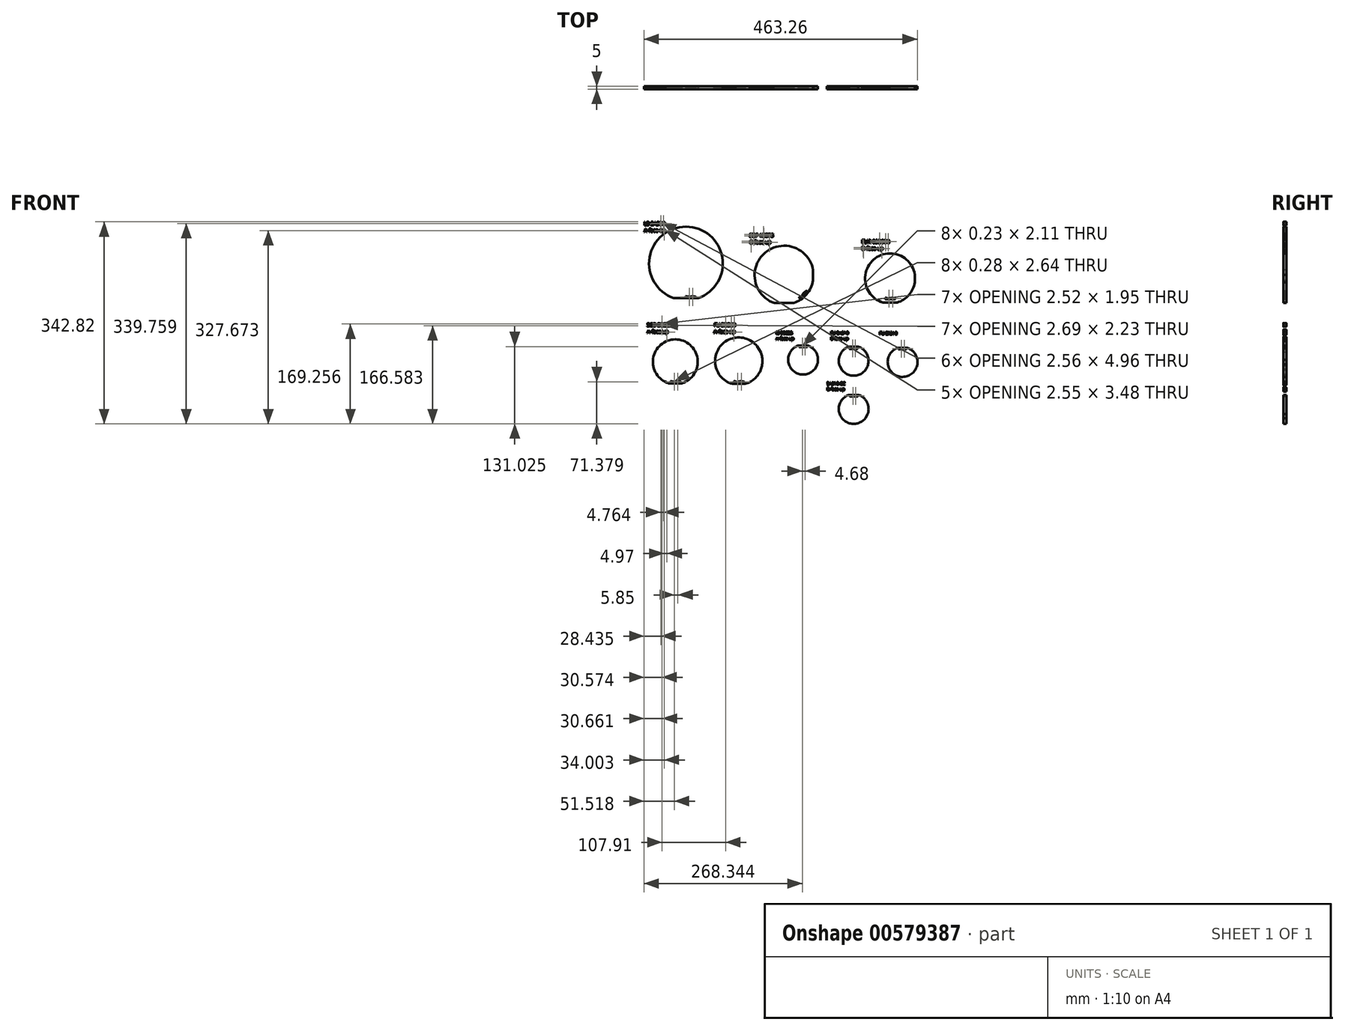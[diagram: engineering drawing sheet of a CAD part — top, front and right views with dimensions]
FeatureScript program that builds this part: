
annotation { "Feature Type Name" : "Feature", "Feature Type Description" : "" }
export const myFeature = defineFeature(function(context is Context, id is Id, definition is map)
    precondition{}
    {
        {
            var Q0;
            Q0=qCreatedBy(makeId("Front.planeOp"),FACE);
            var sketch = newSketch(context, id + "F0", { "sketchPlane" : qUnion([Q0])});
            skArc(sketch, "E0", {"start": v(21, -58.87) * mm, "mid": v(0, 62.5) * mm, "end": v(-21, -58.87) * mm});
            skLineSegment(sketch, "E1", {"start": v(0, -58.87) * mm, "end": v(21, -58.87) * mm});
            skLineSegment(sketch, "E2", {"start": v(21, -58.87) * mm, "end": v(-21, -58.87) * mm});
            skPoint(sketch, "E3.orphan", {"position": v(0, 62.5) * mm});
            skLineSegment(sketch, "E4", {"start": v(0, -58.87) * mm, "end": v(0, -57.87) * mm});
            skText(sketch, "E5", { "text": "Boule-Slice", "fontName": "OpenSans-Regular.ttf"});
            skText(sketch, "E6", { "text": "L3 5A900\nA-face up", "fontName": "OpenSans-Regular.ttf"});
            const initialGuessF0  = {"E5": [-0.00118, -0.05786, 1, 0, 0.0025], "E6": [-0.08084, 0.06549, 1, 0, 0.006]};
            skSetInitialGuess(sketch, initialGuessF0);
            skSolve(sketch);
        }
        {
            var Q0;
            Q0=qCreatedBy(makeId("Front.planeOp"),FACE);
            var sketch = newSketch(context, id + "F1", { "sketchPlane" : qUnion([Q0])});
            skArc(sketch, "E7", {"start": v(182.66, -67.08) * mm, "mid": v(204.4, -52.3) * mm, "end": v(215.64, -28.54) * mm});
            skLineSegment(sketch, "E8", {"start": v(182.66, -67.08) * mm, "end": v(150.16, -67.08) * mm});
            skText(sketch, "E9", { "text": "Boule-Slice", "fontName": "OpenSans-Regular.ttf"});
            skLineSegment(sketch, "E10", {"start": v(215.64, -19.31) * mm, "end": v(215.64, -28.54) * mm});
            skLineSegment(sketch, "E11", {"start": v(215.64, -28.54) * mm, "end": v(215.64, -11.04) * mm});
            skArc(sketch, "E12.trimOffspring", {"start": v(215.64, -11.04) * mm, "mid": v(133.9, 18.2) * mm, "end": v(150.16, -67.08) * mm});
            skArc(sketch, "E13", {"start": v(358.04, -66.17) * mm, "mid": v(378.01, -53.4) * mm, "end": v(388.04, -31.9) * mm});
            skLineSegment(sketch, "E14", {"start": v(358.04, -66.17) * mm, "end": v(334.04, -66.17) * mm});
            skText(sketch, "E15", { "text": "Boule-Slice", "fontName": "OpenSans-Regular.ttf"});
            skLineSegment(sketch, "E16", {"start": v(388.04, -31.9) * mm, "end": v(388.04, -18.9) * mm});
            skArc(sketch, "E17.trimOffspring", {"start": v(388.04, -18.9) * mm, "mid": v(318.04, 6.58) * mm, "end": v(334.04, -66.17) * mm});
            skText(sketch, "E18", { "text": "L3 5A900\nA-face up", "fontName": "OpenSans-Regular.ttf"});
            skText(sketch, "E19", { "text": "SBF 4B875\nB-face up", "fontName": "OpenSans-Regular.ttf"});
            skText(sketch, "E20", { "text": "FLIR 85B900\nB-face up", "fontName": "OpenSans-Regular.ttf"});
            skLineSegment(sketch, "E21", {"start": v(-9.02, -203.08) * mm, "end": v(-7.02, -203.08) * mm});
            skLineSegment(sketch, "E22", {"start": v(-7.02, -203.08) * mm, "end": v(-29.02, -203.08) * mm});
            skText(sketch, "E23", { "text": "Boule-Slice", "fontName": "OpenSans-Regular.ttf"});
            skText(sketch, "E24", { "text": "SCD 3B825\nA-face up", "fontName": "OpenSans-Regular.ttf"});
            skArc(sketch, "E25", {"start": v(-7.02, -203.08) * mm, "mid": v(-18.02, -128.71) * mm, "end": v(-29.02, -203.08) * mm});
            skText(sketch, "E26", { "text": "Boule-Slice", "fontName": "OpenSans-Regular.ttf"});
            skText(sketch, "E27", { "text": "FU 3B800\nA-face up", "fontName": "OpenSans-Regular.ttf"});
            skArc(sketch, "E28", {"start": v(120.92, -140.52) * mm, "mid": v(56.1, -143.31) * mm, "end": v(78.53, -204.2) * mm});
            skLineSegment(sketch, "E29", {"start": v(120.92, -140.52) * mm, "end": v(126.92, -150.9) * mm});
            skLineSegment(sketch, "E30", {"start": v(100.53, -204.2) * mm, "end": v(78.53, -204.2) * mm});
            skArc(sketch, "E31.trimOffspring", {"start": v(100.53, -204.2) * mm, "mid": v(125.52, -183.4) * mm, "end": v(126.92, -150.9) * mm});
            const initialGuessF1  = {"E9": [0.193, -0.05963, 0.7071, 0.7071, 0.0025], "E15": [0.33754, -0.06053, 1, 0, 0.0025], "E18": [-0.07111, 0.06484, 1, 0, 0.006], "E19": [0.10778, 0.04488, 1, 0, 0.006], "E20": [0.29791, 0.0343, 1, 0, 0.006], "E23": [-0.02651, -0.20188, 1, 0, 0.0025], "E24": [-0.06614, -0.10706, 1, 0, 0.006], "E26": [0.08103, -0.20188, 1, 0, 0.0025], "E27": [0.04731, -0.10706, 1, 0, 0.006]};
            skSetInitialGuess(sketch, initialGuessF1);
            skSolve(sketch);
        }
        {
            var Q0;
            Q0=qCreatedBy(makeId("Front.planeOp"),FACE);
            var sketch = newSketch(context, id + "F2", { "sketchPlane" : qUnion([Q0])});
            skArc(sketch, "E32", {"start": v(222.18, -172.07) * mm, "mid": v(221.52, -152.51) * mm, "end": v(207.09, -139.3) * mm});
            skLineSegment(sketch, "E33", {"start": v(222.18, -172.07) * mm, "end": v(218.18, -179) * mm});
            skLineSegment(sketch, "E34", {"start": v(207.09, -139.3) * mm, "end": v(190.09, -139.3) * mm});
            skArc(sketch, "E35.trimOffspring", {"start": v(190.09, -139.3) * mm, "mid": v(177.97, -177.66) * mm, "end": v(218.18, -179) * mm});
            skText(sketch, "E36", { "text": "Boule-Slice", "fontName": "OpenSans-Regular.ttf"});
            skText(sketch, "E37", { "text": "i3 2B625\nA-face up", "fontName": "OpenSans-Regular.ttf"});
            skText(sketch, "E38", { "text": "FU 2A510\nB-face up", "fontName": "OpenSans-Regular.ttf"});
            skLineSegment(sketch, "E39.MirrorCS", {"start": v(260.72, -174.09) * mm, "end": v(264.72, -181.01) * mm});
            skLineSegment(sketch, "E40.MirrorCS", {"start": v(276.31, -141.13) * mm, "end": v(292.31, -141.13) * mm});
            skArc(sketch, "E41.MirrorCS", {"start": v(260.72, -174.09) * mm, "mid": v(261.5, -154.28) * mm, "end": v(276.31, -141.13) * mm});
            skArc(sketch, "E42.MirrorCS", {"start": v(292.31, -141.13) * mm, "mid": v(305.08, -179.45) * mm, "end": v(264.72, -181.01) * mm});
            skText(sketch, "E43", { "text": "Boule-Slice", "fontName": "OpenSans-Regular.ttf"});
            skPoint(sketch, "E44", {"position": v(192.9, -141.97) * mm});
            skText(sketch, "E45", { "text": "FU 2X510\n", "fontName": "OpenSans-Regular.ttf"});
            skLineSegment(sketch, "E46.MirrorCS", {"start": v(359.22, -143.15) * mm, "end": v(375.22, -143.15) * mm});
            skText(sketch, "E47", { "text": "Boule-Slice", "fontName": "OpenSans-Regular.ttf"});
            skLineSegment(sketch, "E48", {"start": v(392.15, -171.1) * mm, "end": v(392.15, -163.1) * mm});
            skArc(sketch, "E49", {"start": v(359.22, -143.15) * mm, "mid": v(350.88, -186.35) * mm, "end": v(392.15, -171.1) * mm});
            skArc(sketch, "E50.trimOffspring", {"start": v(392.15, -163.1) * mm, "mid": v(386.47, -150.76) * mm, "end": v(375.22, -143.15) * mm});
            skArc(sketch, "E51", {"start": v(307.95, -255.69) * mm, "mid": v(307.29, -236.13) * mm, "end": v(292.85, -222.9) * mm});
            skLineSegment(sketch, "E52", {"start": v(307.95, -255.69) * mm, "end": v(303.95, -262.62) * mm});
            skLineSegment(sketch, "E53", {"start": v(292.85, -222.9) * mm, "end": v(275.85, -222.9) * mm});
            skArc(sketch, "E54.trimOffspring", {"start": v(275.85, -222.9) * mm, "mid": v(263.74, -261.27) * mm, "end": v(303.95, -262.62) * mm});
            skText(sketch, "E55", { "text": "Boule-Slice", "fontName": "OpenSans-Regular.ttf"});
            skPoint(sketch, "E56", {"position": v(278.67, -225.58) * mm});
            skText(sketch, "E57", { "text": "2A510-CC\nB-face up", "fontName": "OpenSans-Regular.ttf"});
            const initialGuessF2  = {"E36": [0.1917, -0.14197, 1, 0, 0.002], "E37": [0.1527, -0.12022, 1, 0, 0.005], "E38": [0.24497, -0.12022, 1, 0, 0.005], "E43": [0.2769, -0.14481, 1, 0, 0.002], "E45": [0.32788, -0.12073, 1, 0, 0.005], "E47": [0.3598, -0.14532, 1, 0, 0.002], "E55": [0.27747, -0.22558, 1, 0, 0.002], "E57": [0.23866, -0.20613, 1, 0, 0.005]};
            skSetInitialGuess(sketch, initialGuessF2);
            skSolve(sketch);
        }
        {
            var Q0;
            {var subQ1=sQuery(id+"F0.wireOp",EDGE,"E0");Q0=makeQuery(id+"F0.imprint","IMPRINT",FACE,{"disambiguationData":[TD([[makeQuery(id+"F0.imprint","IMPRINT",EDGE,{"derivedFrom":subQ1}),1.0]])]});}
            var Q1;
            Q1=makeQuery(id+"F0.imprint","IMPRINT",FACE,{"disambiguationData":[TD([[makeQuery(id+"F0.imprint","IMPRINT",EDGE,{"derivedFrom":sQuery(id+"F0.wireOp",EDGE,"E5.sketch_text.stroke-77")}),1.0]])]});
            var Q2;
            Q2=makeQuery(id+"F0.imprint","IMPRINT",FACE,{"disambiguationData":[TD([[makeQuery(id+"F0.imprint","IMPRINT",EDGE,{"derivedFrom":sQuery(id+"F0.wireOp",EDGE,"E5.sketch_text.stroke-156")}),1.0]])]});
            var Q3;
            Q3=makeQuery(id+"F0.imprint","IMPRINT",FACE,{"disambiguationData":[TD([[makeQuery(id+"F0.imprint","IMPRINT",EDGE,{"derivedFrom":sQuery(id+"F0.wireOp",EDGE,"E5.sketch_text.stroke-11")}),1.0]])]});
            var Q4;
            Q4=makeQuery(id+"F0.imprint","IMPRINT",FACE,{"disambiguationData":[TD([[makeQuery(id+"F0.imprint","IMPRINT",EDGE,{"derivedFrom":sQuery(id+"F0.wireOp",EDGE,"E5.sketch_text.stroke-18")}),1.0]])]});
            var Q5;
            Q5=makeQuery(id+"F0.imprint","IMPRINT",FACE,{"disambiguationData":[TD([[makeQuery(id+"F0.imprint","IMPRINT",EDGE,{"derivedFrom":sQuery(id+"F0.wireOp",EDGE,"E5.sketch_text.stroke-34")}),1.0]])]});
            var Q6;
            Q6=makeQuery(id+"F1.imprint","IMPRINT",FACE,{"disambiguationData":[TD([[makeQuery(id+"F1.imprint","IMPRINT",EDGE,{"derivedFrom":sQuery(id+"F1.wireOp",EDGE,"E18.sketch_text.stroke-0")}),-1.0]])]});
            var Q7;
            Q7=makeQuery(id+"F1.imprint","IMPRINT",FACE,{"disambiguationData":[TD([[makeQuery(id+"F1.imprint","IMPRINT",EDGE,{"derivedFrom":sQuery(id+"F1.wireOp",EDGE,"E18.sketch_text.stroke-6")}),-1.0]])]});
            var Q8;
            Q8=makeQuery(id+"F1.imprint","IMPRINT",FACE,{"disambiguationData":[TD([[makeQuery(id+"F1.imprint","IMPRINT",EDGE,{"derivedFrom":sQuery(id+"F1.wireOp",EDGE,"E18.sketch_text.stroke-34")}),-1.0]])]});
            var Q9;
            Q9=makeQuery(id+"F1.imprint","IMPRINT",FACE,{"disambiguationData":[TD([[makeQuery(id+"F1.imprint","IMPRINT",EDGE,{"derivedFrom":sQuery(id+"F1.wireOp",EDGE,"E18.sketch_text.stroke-137")}),-1.0]])]});
            var Q10;
            Q10=makeQuery(id+"F1.imprint","IMPRINT",FACE,{"disambiguationData":[TD([[makeQuery(id+"F1.imprint","IMPRINT",EDGE,{"derivedFrom":sQuery(id+"F1.wireOp",EDGE,"E18.sketch_text.stroke-141")}),-1.0]])]});
            var Q11;
            Q11=makeQuery(id+"F1.imprint","IMPRINT",FACE,{"disambiguationData":[TD([[makeQuery(id+"F1.imprint","IMPRINT",EDGE,{"derivedFrom":sQuery(id+"F1.wireOp",EDGE,"E18.sketch_text.stroke-185")}),-1.0]])]});
            var Q12;
            Q12=makeQuery(id+"F1.imprint","IMPRINT",FACE,{"disambiguationData":[TD([[makeQuery(id+"F1.imprint","IMPRINT",EDGE,{"derivedFrom":sQuery(id+"F1.wireOp",EDGE,"E18.sketch_text.stroke-219")}),-1.0]])]});
            var Q13;
            Q13=makeQuery(id+"F1.imprint","IMPRINT",FACE,{"disambiguationData":[TD([[makeQuery(id+"F1.imprint","IMPRINT",EDGE,{"derivedFrom":sQuery(id+"F1.wireOp",EDGE,"E19.sketch_text.stroke-0")}),-1.0]])]});
            var Q14;
            Q14=makeQuery(id+"F1.imprint","IMPRINT",FACE,{"disambiguationData":[TD([[makeQuery(id+"F1.imprint","IMPRINT",EDGE,{"derivedFrom":sQuery(id+"F1.wireOp",EDGE,"E19.sketch_text.stroke-50")}),-1.0]])]});
            var Q15;
            Q15=makeQuery(id+"F1.imprint","IMPRINT",FACE,{"disambiguationData":[TD([[makeQuery(id+"F1.imprint","IMPRINT",EDGE,{"derivedFrom":sQuery(id+"F1.wireOp",EDGE,"E19.sketch_text.stroke-133")}),-1.0]])]});
            var Q16;
            Q16=makeQuery(id+"F1.imprint","IMPRINT",FACE,{"disambiguationData":[TD([[makeQuery(id+"F1.imprint","IMPRINT",EDGE,{"derivedFrom":sQuery(id+"F1.wireOp",EDGE,"E19.sketch_text.stroke-140")}),-1.0]])]});
            var Q17;
            Q17=makeQuery(id+"F1.imprint","IMPRINT",FACE,{"disambiguationData":[TD([[makeQuery(id+"F1.imprint","IMPRINT",EDGE,{"derivedFrom":sQuery(id+"F1.wireOp",EDGE,"E19.sketch_text.stroke-184")}),-1.0]])]});
            var Q18;
            Q18=makeQuery(id+"F1.imprint","IMPRINT",FACE,{"disambiguationData":[TD([[makeQuery(id+"F1.imprint","IMPRINT",EDGE,{"derivedFrom":sQuery(id+"F1.wireOp",EDGE,"E19.sketch_text.stroke-188")}),-1.0]])]});
            var Q19;
            Q19=makeQuery(id+"F1.imprint","IMPRINT",FACE,{"disambiguationData":[TD([[makeQuery(id+"F1.imprint","IMPRINT",EDGE,{"derivedFrom":sQuery(id+"F1.wireOp",EDGE,"E19.sketch_text.stroke-232")}),-1.0]])]});
            var Q20;
            Q20=makeQuery(id+"F1.imprint","IMPRINT",FACE,{"disambiguationData":[TD([[makeQuery(id+"F1.imprint","IMPRINT",EDGE,{"derivedFrom":sQuery(id+"F1.wireOp",EDGE,"E19.sketch_text.stroke-266")}),-1.0]])]});
            var Q21;
            Q21=makeQuery(id+"F1.imprint","IMPRINT",FACE,{"disambiguationData":[TD([[makeQuery(id+"F1.imprint","IMPRINT",EDGE,{"derivedFrom":sQuery(id+"F1.wireOp",EDGE,"E20.sketch_text.stroke-0")}),-1.0]])]});
            var Q22;
            Q22=makeQuery(id+"F1.imprint","IMPRINT",FACE,{"disambiguationData":[TD([[makeQuery(id+"F1.imprint","IMPRINT",EDGE,{"derivedFrom":sQuery(id+"F1.wireOp",EDGE,"E20.sketch_text.stroke-10")}),-1.0]])]});
            var Q23;
            Q23=makeQuery(id+"F1.imprint","IMPRINT",FACE,{"disambiguationData":[TD([[makeQuery(id+"F1.imprint","IMPRINT",EDGE,{"derivedFrom":sQuery(id+"F1.wireOp",EDGE,"E20.sketch_text.stroke-16")}),-1.0]])]});
            var Q24;
            Q24=makeQuery(id+"F1.imprint","IMPRINT",FACE,{"disambiguationData":[TD([[makeQuery(id+"F1.imprint","IMPRINT",EDGE,{"derivedFrom":sQuery(id+"F1.wireOp",EDGE,"E20.sketch_text.stroke-69")}),-1.0]])]});
            var Q25;
            Q25=makeQuery(id+"F1.imprint","IMPRINT",FACE,{"disambiguationData":[TD([[makeQuery(id+"F1.imprint","IMPRINT",EDGE,{"derivedFrom":sQuery(id+"F1.wireOp",EDGE,"E20.sketch_text.stroke-196")}),-1.0]])]});
            var Q26;
            Q26=makeQuery(id+"F1.imprint","IMPRINT",FACE,{"disambiguationData":[TD([[makeQuery(id+"F1.imprint","IMPRINT",EDGE,{"derivedFrom":sQuery(id+"F1.wireOp",EDGE,"E20.sketch_text.stroke-200")}),-1.0]])]});
            var Q27;
            Q27=makeQuery(id+"F1.imprint","IMPRINT",FACE,{"disambiguationData":[TD([[makeQuery(id+"F1.imprint","IMPRINT",EDGE,{"derivedFrom":sQuery(id+"F1.wireOp",EDGE,"E20.sketch_text.stroke-244")}),-1.0]])]});
            var Q28;
            Q28=makeQuery(id+"F1.imprint","IMPRINT",FACE,{"disambiguationData":[TD([[makeQuery(id+"F1.imprint","IMPRINT",EDGE,{"derivedFrom":sQuery(id+"F1.wireOp",EDGE,"E20.sketch_text.stroke-278")}),-1.0]])]});
            var Q29;
            Q29=makeQuery(id+"F1.imprint","IMPRINT",FACE,{"disambiguationData":[TD([[makeQuery(id+"F1.imprint","IMPRINT",EDGE,{"derivedFrom":sQuery(id+"F1.wireOp",EDGE,"E24.sketch_text.stroke-0")}),-1.0]])]});
            var Q30;
            Q30=makeQuery(id+"F1.imprint","IMPRINT",FACE,{"disambiguationData":[TD([[makeQuery(id+"F1.imprint","IMPRINT",EDGE,{"derivedFrom":sQuery(id+"F1.wireOp",EDGE,"E24.sketch_text.stroke-25")}),-1.0]])]});
            var Q31;
            Q31=makeQuery(id+"F1.imprint","IMPRINT",FACE,{"disambiguationData":[TD([[makeQuery(id+"F1.imprint","IMPRINT",EDGE,{"derivedFrom":sQuery(id+"F1.wireOp",EDGE,"E24.sketch_text.stroke-54")}),-1.0]])]});
            var Q32;
            Q32=makeQuery(id+"F1.imprint","IMPRINT",FACE,{"disambiguationData":[TD([[makeQuery(id+"F1.imprint","IMPRINT",EDGE,{"derivedFrom":sQuery(id+"F1.wireOp",EDGE,"E24.sketch_text.stroke-138")}),-1.0]])]});
            var Q33;
            Q33=makeQuery(id+"F1.imprint","IMPRINT",FACE,{"disambiguationData":[TD([[makeQuery(id+"F1.imprint","IMPRINT",EDGE,{"derivedFrom":sQuery(id+"F1.wireOp",EDGE,"E24.sketch_text.stroke-158")}),-1.0]])]});
            var Q34;
            Q34=makeQuery(id+"F1.imprint","IMPRINT",FACE,{"disambiguationData":[TD([[makeQuery(id+"F1.imprint","IMPRINT",EDGE,{"derivedFrom":sQuery(id+"F1.wireOp",EDGE,"E24.sketch_text.stroke-190")}),-1.0]])]});
            var Q35;
            Q35=makeQuery(id+"F1.imprint","IMPRINT",FACE,{"disambiguationData":[TD([[makeQuery(id+"F1.imprint","IMPRINT",EDGE,{"derivedFrom":sQuery(id+"F1.wireOp",EDGE,"E24.sketch_text.stroke-194")}),-1.0]])]});
            var Q36;
            Q36=makeQuery(id+"F1.imprint","IMPRINT",FACE,{"disambiguationData":[TD([[makeQuery(id+"F1.imprint","IMPRINT",EDGE,{"derivedFrom":sQuery(id+"F1.wireOp",EDGE,"E24.sketch_text.stroke-238")}),-1.0]])]});
            var Q37;
            Q37=makeQuery(id+"F1.imprint","IMPRINT",FACE,{"disambiguationData":[TD([[makeQuery(id+"F1.imprint","IMPRINT",EDGE,{"derivedFrom":sQuery(id+"F1.wireOp",EDGE,"E24.sketch_text.stroke-272")}),-1.0]])]});
            var Q38;
            Q38=makeQuery(id+"F1.imprint","IMPRINT",FACE,{"disambiguationData":[TD([[makeQuery(id+"F1.imprint","IMPRINT",EDGE,{"derivedFrom":sQuery(id+"F1.wireOp",EDGE,"E27.sketch_text.stroke-0")}),-1.0]])]});
            var Q39;
            Q39=makeQuery(id+"F1.imprint","IMPRINT",FACE,{"disambiguationData":[TD([[makeQuery(id+"F1.imprint","IMPRINT",EDGE,{"derivedFrom":sQuery(id+"F1.wireOp",EDGE,"E27.sketch_text.stroke-10")}),-1.0]])]});
            var Q40;
            Q40=makeQuery(id+"F1.imprint","IMPRINT",FACE,{"disambiguationData":[TD([[makeQuery(id+"F1.imprint","IMPRINT",EDGE,{"derivedFrom":sQuery(id+"F1.wireOp",EDGE,"E27.sketch_text.stroke-24")}),-1.0]])]});
            var Q41;
            Q41=makeQuery(id+"F1.imprint","IMPRINT",FACE,{"disambiguationData":[TD([[makeQuery(id+"F1.imprint","IMPRINT",EDGE,{"derivedFrom":sQuery(id+"F1.wireOp",EDGE,"E27.sketch_text.stroke-153")}),-1.0]])]});
            var Q42;
            Q42=makeQuery(id+"F1.imprint","IMPRINT",FACE,{"disambiguationData":[TD([[makeQuery(id+"F1.imprint","IMPRINT",EDGE,{"derivedFrom":sQuery(id+"F1.wireOp",EDGE,"E27.sketch_text.stroke-157")}),-1.0]])]});
            var Q43;
            Q43=makeQuery(id+"F1.imprint","IMPRINT",FACE,{"disambiguationData":[TD([[makeQuery(id+"F1.imprint","IMPRINT",EDGE,{"derivedFrom":sQuery(id+"F1.wireOp",EDGE,"E27.sketch_text.stroke-201")}),-1.0]])]});
            var Q44;
            Q44=makeQuery(id+"F1.imprint","IMPRINT",FACE,{"disambiguationData":[TD([[makeQuery(id+"F1.imprint","IMPRINT",EDGE,{"derivedFrom":sQuery(id+"F1.wireOp",EDGE,"E27.sketch_text.stroke-235")}),-1.0]])]});
            var Q45;
            Q45=makeQuery(id+"F1.imprint","IMPRINT",FACE,{"disambiguationData":[TD([[makeQuery(id+"F1.imprint","IMPRINT",EDGE,{"derivedFrom":sQuery(id+"F1.wireOp",EDGE,"E18.sketch_text.stroke-53")}),-1.0]])]});
            var Q46;
            Q46=makeQuery(id+"F1.imprint","IMPRINT",FACE,{"disambiguationData":[TD([[makeQuery(id+"F1.imprint","IMPRINT",EDGE,{"derivedFrom":sQuery(id+"F1.wireOp",EDGE,"E18.sketch_text.stroke-66")}),-1.0]])]});
            var Q47;
            Q47=makeQuery(id+"F1.imprint","IMPRINT",FACE,{"disambiguationData":[TD([[makeQuery(id+"F1.imprint","IMPRINT",EDGE,{"derivedFrom":sQuery(id+"F1.wireOp",EDGE,"E18.sketch_text.stroke-92")}),-1.0]])]});
            var Q48;
            Q48=makeQuery(id+"F1.imprint","IMPRINT",FACE,{"disambiguationData":[TD([[makeQuery(id+"F1.imprint","IMPRINT",EDGE,{"derivedFrom":sQuery(id+"F1.wireOp",EDGE,"E18.sketch_text.stroke-108")}),-1.0]])]});
            var Q49;
            Q49=makeQuery(id+"F1.imprint","IMPRINT",FACE,{"disambiguationData":[TD([[makeQuery(id+"F1.imprint","IMPRINT",EDGE,{"derivedFrom":sQuery(id+"F1.wireOp",EDGE,"E18.sketch_text.stroke-124")}),-1.0]])]});
            var Q50;
            Q50=makeQuery(id+"F1.imprint","IMPRINT",FACE,{"disambiguationData":[TD([[makeQuery(id+"F1.imprint","IMPRINT",EDGE,{"derivedFrom":sQuery(id+"F1.wireOp",EDGE,"E18.sketch_text.stroke-158")}),-1.0]])]});
            var Q51;
            Q51=makeQuery(id+"F1.imprint","IMPRINT",FACE,{"disambiguationData":[TD([[makeQuery(id+"F1.imprint","IMPRINT",EDGE,{"derivedFrom":sQuery(id+"F1.wireOp",EDGE,"E18.sketch_text.stroke-200")}),-1.0]])]});
            var Q52;
            Q52=makeQuery(id+"F1.imprint","IMPRINT",FACE,{"disambiguationData":[TD([[makeQuery(id+"F1.imprint","IMPRINT",EDGE,{"derivedFrom":sQuery(id+"F1.wireOp",EDGE,"E18.sketch_text.stroke-236")}),-1.0]])]});
            var Q53;
            Q53=makeQuery(id+"F1.imprint","IMPRINT",FACE,{"disambiguationData":[TD([[makeQuery(id+"F1.imprint","IMPRINT",EDGE,{"derivedFrom":sQuery(id+"F1.wireOp",EDGE,"E19.sketch_text.stroke-60")}),-1.0]])]});
            var Q54;
            Q54=makeQuery(id+"F1.imprint","IMPRINT",FACE,{"disambiguationData":[TD([[makeQuery(id+"F1.imprint","IMPRINT",EDGE,{"derivedFrom":sQuery(id+"F1.wireOp",EDGE,"E19.sketch_text.stroke-205")}),-1.0]])]});
            var Q55;
            Q55=makeQuery(id+"F1.imprint","IMPRINT",FACE,{"disambiguationData":[TD([[makeQuery(id+"F1.imprint","IMPRINT",EDGE,{"derivedFrom":sQuery(id+"F1.wireOp",EDGE,"E19.sketch_text.stroke-247")}),-1.0]])]});
            var Q56;
            Q56=makeQuery(id+"F1.imprint","IMPRINT",FACE,{"disambiguationData":[TD([[makeQuery(id+"F1.imprint","IMPRINT",EDGE,{"derivedFrom":sQuery(id+"F1.wireOp",EDGE,"E19.sketch_text.stroke-283")}),-1.0]])]});
            var Q57;
            Q57=makeQuery(id+"F1.imprint","IMPRINT",FACE,{"disambiguationData":[TD([[makeQuery(id+"F1.imprint","IMPRINT",EDGE,{"derivedFrom":sQuery(id+"F1.wireOp",EDGE,"E20.sketch_text.stroke-20")}),-1.0]])]});
            var Q58;
            Q58=makeQuery(id+"F1.imprint","IMPRINT",FACE,{"disambiguationData":[TD([[makeQuery(id+"F1.imprint","IMPRINT",EDGE,{"derivedFrom":sQuery(id+"F1.wireOp",EDGE,"E20.sketch_text.stroke-113")}),-1.0]])]});
            var Q59;
            Q59=makeQuery(id+"F1.imprint","IMPRINT",FACE,{"disambiguationData":[TD([[makeQuery(id+"F1.imprint","IMPRINT",EDGE,{"derivedFrom":sQuery(id+"F1.wireOp",EDGE,"E20.sketch_text.stroke-139")}),-1.0]])]});
            var Q60;
            Q60=makeQuery(id+"F1.imprint","IMPRINT",FACE,{"disambiguationData":[TD([[makeQuery(id+"F1.imprint","IMPRINT",EDGE,{"derivedFrom":sQuery(id+"F1.wireOp",EDGE,"E20.sketch_text.stroke-155")}),-1.0]])]});
            var Q61;
            Q61=makeQuery(id+"F1.imprint","IMPRINT",FACE,{"disambiguationData":[TD([[makeQuery(id+"F1.imprint","IMPRINT",EDGE,{"derivedFrom":sQuery(id+"F1.wireOp",EDGE,"E20.sketch_text.stroke-217")}),-1.0]])]});
            var Q62;
            Q62=makeQuery(id+"F1.imprint","IMPRINT",FACE,{"disambiguationData":[TD([[makeQuery(id+"F1.imprint","IMPRINT",EDGE,{"derivedFrom":sQuery(id+"F1.wireOp",EDGE,"E20.sketch_text.stroke-259")}),-1.0]])]});
            var Q63;
            Q63=makeQuery(id+"F1.imprint","IMPRINT",FACE,{"disambiguationData":[TD([[makeQuery(id+"F1.imprint","IMPRINT",EDGE,{"derivedFrom":sQuery(id+"F1.wireOp",EDGE,"E20.sketch_text.stroke-295")}),-1.0]])]});
            var Q64;
            Q64=makeQuery(id+"F1.imprint","IMPRINT",FACE,{"disambiguationData":[TD([[makeQuery(id+"F1.imprint","IMPRINT",EDGE,{"derivedFrom":sQuery(id+"F1.wireOp",EDGE,"E24.sketch_text.stroke-40")}),-1.0]])]});
            var Q65;
            Q65=makeQuery(id+"F1.imprint","IMPRINT",FACE,{"disambiguationData":[TD([[makeQuery(id+"F1.imprint","IMPRINT",EDGE,{"derivedFrom":sQuery(id+"F1.wireOp",EDGE,"E24.sketch_text.stroke-177")}),-1.0]])]});
            var Q66;
            Q66=makeQuery(id+"F1.imprint","IMPRINT",FACE,{"disambiguationData":[TD([[makeQuery(id+"F1.imprint","IMPRINT",EDGE,{"derivedFrom":sQuery(id+"F1.wireOp",EDGE,"E24.sketch_text.stroke-211")}),-1.0]])]});
            var Q67;
            Q67=makeQuery(id+"F1.imprint","IMPRINT",FACE,{"disambiguationData":[TD([[makeQuery(id+"F1.imprint","IMPRINT",EDGE,{"derivedFrom":sQuery(id+"F1.wireOp",EDGE,"E24.sketch_text.stroke-253")}),-1.0]])]});
            var Q68;
            Q68=makeQuery(id+"F1.imprint","IMPRINT",FACE,{"disambiguationData":[TD([[makeQuery(id+"F1.imprint","IMPRINT",EDGE,{"derivedFrom":sQuery(id+"F1.wireOp",EDGE,"E24.sketch_text.stroke-289")}),-1.0]])]});
            var Q69;
            Q69=makeQuery(id+"F1.imprint","IMPRINT",FACE,{"disambiguationData":[TD([[makeQuery(id+"F1.imprint","IMPRINT",EDGE,{"derivedFrom":sQuery(id+"F1.wireOp",EDGE,"E27.sketch_text.stroke-108")}),-1.0]])]});
            var Q70;
            Q70=makeQuery(id+"F1.imprint","IMPRINT",FACE,{"disambiguationData":[TD([[makeQuery(id+"F1.imprint","IMPRINT",EDGE,{"derivedFrom":sQuery(id+"F1.wireOp",EDGE,"E27.sketch_text.stroke-124")}),-1.0]])]});
            var Q71;
            Q71=makeQuery(id+"F1.imprint","IMPRINT",FACE,{"disambiguationData":[TD([[makeQuery(id+"F1.imprint","IMPRINT",EDGE,{"derivedFrom":sQuery(id+"F1.wireOp",EDGE,"E27.sketch_text.stroke-140")}),-1.0]])]});
            var Q72;
            Q72=makeQuery(id+"F1.imprint","IMPRINT",FACE,{"disambiguationData":[TD([[makeQuery(id+"F1.imprint","IMPRINT",EDGE,{"derivedFrom":sQuery(id+"F1.wireOp",EDGE,"E27.sketch_text.stroke-174")}),-1.0]])]});
            var Q73;
            Q73=makeQuery(id+"F1.imprint","IMPRINT",FACE,{"disambiguationData":[TD([[makeQuery(id+"F1.imprint","IMPRINT",EDGE,{"derivedFrom":sQuery(id+"F1.wireOp",EDGE,"E27.sketch_text.stroke-216")}),-1.0]])]});
            var Q74;
            Q74=makeQuery(id+"F1.imprint","IMPRINT",FACE,{"disambiguationData":[TD([[makeQuery(id+"F1.imprint","IMPRINT",EDGE,{"derivedFrom":sQuery(id+"F1.wireOp",EDGE,"E27.sketch_text.stroke-252")}),-1.0]])]});
            var Q75;
            Q75=makeQuery(id+"F1.imprint","IMPRINT",FACE,{"disambiguationData":[TD([[makeQuery(id+"F1.imprint","IMPRINT",EDGE,{"derivedFrom":sQuery(id+"F1.wireOp",EDGE,"E19.sketch_text.stroke-25")}),-1.0]])]});
            var Q76;
            Q76=makeQuery(id+"F1.imprint","IMPRINT",FACE,{"disambiguationData":[TD([[makeQuery(id+"F1.imprint","IMPRINT",EDGE,{"derivedFrom":sQuery(id+"F1.wireOp",EDGE,"E19.sketch_text.stroke-77")}),-1.0]])]});
            var Q77;
            Q77=makeQuery(id+"F1.imprint","IMPRINT",FACE,{"disambiguationData":[TD([[makeQuery(id+"F1.imprint","IMPRINT",EDGE,{"derivedFrom":sQuery(id+"F1.wireOp",EDGE,"E19.sketch_text.stroke-102")}),-1.0]])]});
            var Q78;
            Q78=makeQuery(id+"F1.imprint","IMPRINT",FACE,{"disambiguationData":[TD([[makeQuery(id+"F1.imprint","IMPRINT",EDGE,{"derivedFrom":sQuery(id+"F1.wireOp",EDGE,"E19.sketch_text.stroke-159")}),-1.0]])]});
            var Q79;
            Q79=makeQuery(id+"F1.imprint","IMPRINT",FACE,{"disambiguationData":[TD([[makeQuery(id+"F1.imprint","IMPRINT",EDGE,{"derivedFrom":sQuery(id+"F1.wireOp",EDGE,"E20.sketch_text.stroke-38")}),-1.0]])]});
            var Q80;
            Q80=makeQuery(id+"F1.imprint","IMPRINT",FACE,{"disambiguationData":[TD([[makeQuery(id+"F1.imprint","IMPRINT",EDGE,{"derivedFrom":sQuery(id+"F1.wireOp",EDGE,"E20.sketch_text.stroke-88")}),-1.0]])]});
            var Q81;
            Q81=makeQuery(id+"F1.imprint","IMPRINT",FACE,{"disambiguationData":[TD([[makeQuery(id+"F1.imprint","IMPRINT",EDGE,{"derivedFrom":sQuery(id+"F1.wireOp",EDGE,"E20.sketch_text.stroke-171")}),-1.0]])]});
            var Q82;
            Q82=makeQuery(id+"F1.imprint","IMPRINT",FACE,{"disambiguationData":[TD([[makeQuery(id+"F1.imprint","IMPRINT",EDGE,{"derivedFrom":sQuery(id+"F1.wireOp",EDGE,"E24.sketch_text.stroke-82")}),-1.0]])]});
            var Q83;
            Q83=makeQuery(id+"F1.imprint","IMPRINT",FACE,{"disambiguationData":[TD([[makeQuery(id+"F1.imprint","IMPRINT",EDGE,{"derivedFrom":sQuery(id+"F1.wireOp",EDGE,"E24.sketch_text.stroke-107")}),-1.0]])]});
            var Q84;
            Q84=makeQuery(id+"F1.imprint","IMPRINT",FACE,{"disambiguationData":[TD([[makeQuery(id+"F1.imprint","IMPRINT",EDGE,{"derivedFrom":sQuery(id+"F1.wireOp",EDGE,"E27.sketch_text.stroke-52")}),-1.0]])]});
            var Q85;
            Q85=makeQuery(id+"F1.imprint","IMPRINT",FACE,{"disambiguationData":[TD([[makeQuery(id+"F1.imprint","IMPRINT",EDGE,{"derivedFrom":sQuery(id+"F1.wireOp",EDGE,"E27.sketch_text.stroke-77")}),-1.0]])]});
            var Q86;
            {var subQ3=sQuery(id+"F1.wireOp",EDGE,"E7");Q86=makeQuery(id+"F1.imprint","IMPRINT",FACE,{"disambiguationData":[TD([[makeQuery(id+"F1.imprint","IMPRINT",EDGE,{"derivedFrom":subQ3}),1.0]])]});}
            var Q87;
            {var subQ3=sQuery(id+"F1.wireOp",EDGE,"E13");Q87=makeQuery(id+"F1.imprint","IMPRINT",FACE,{"disambiguationData":[TD([[makeQuery(id+"F1.imprint","IMPRINT",EDGE,{"derivedFrom":subQ3}),1.0]])]});}
            var Q88;
            Q88=makeQuery(id+"F1.imprint","IMPRINT",FACE,{"disambiguationData":[TD([[makeQuery(id+"F1.imprint","IMPRINT",EDGE,{"derivedFrom":sQuery(id+"F1.wireOp",EDGE,"E23.sketch_text.stroke-0")}),1.0]])]});
            var Q89;
            Q89=makeQuery(id+"F1.imprint","IMPRINT",FACE,{"disambiguationData":[TD([[makeQuery(id+"F1.imprint","IMPRINT",EDGE,{"derivedFrom":sQuery(id+"F1.wireOp",EDGE,"E26.sketch_text.stroke-0")}),1.0]])]});
            var Q90;
            Q90=qSketchRegion(id+"F2",true);
            var Q91;
            Q91=makeQuery(id+"F2.imprint","IMPRINT",FACE,{"disambiguationData":[TD([[makeQuery(id+"F2.imprint","IMPRINT",EDGE,{"derivedFrom":sQuery(id+"F2.wireOp",EDGE,"E36.sketch_text.stroke-34")}),1.0]])]});
            var Q92;
            Q92=makeQuery(id+"F2.imprint","IMPRINT",FACE,{"disambiguationData":[TD([[makeQuery(id+"F2.imprint","IMPRINT",EDGE,{"derivedFrom":sQuery(id+"F2.wireOp",EDGE,"E36.sketch_text.stroke-77")}),1.0]])]});
            var Q93;
            Q93=makeQuery(id+"F2.imprint","IMPRINT",FACE,{"disambiguationData":[TD([[makeQuery(id+"F2.imprint","IMPRINT",EDGE,{"derivedFrom":sQuery(id+"F2.wireOp",EDGE,"E36.sketch_text.stroke-156")}),1.0]])]});
            extrude(context, id + "F3", {"entities" : qUnion([Q0, Q1, Q2, Q3, Q4, Q5, Q6, Q7, Q8, Q9, Q10, Q11, Q12, Q13, Q14, Q15, Q16, Q17, Q18, Q19, Q20, Q21, Q22, Q23, Q24, Q25, Q26, Q27, Q28, Q29, Q30, Q31, Q32, Q33, Q34, Q35, Q36, Q37, Q38, Q39, Q40, Q41, Q42, Q43, Q44, Q45, Q46, Q47, Q48, Q49, Q50, Q51, Q52, Q53, Q54, Q55, Q56, Q57, Q58, Q59, Q60, Q61, Q62, Q63, Q64, Q65, Q66, Q67, Q68, Q69, Q70, Q71, Q72, Q73, Q74, Q75, Q76, Q77, Q78, Q79, Q80, Q81, Q82, Q83, Q84, Q85, Q86, Q87, Q88, Q89, Q90, Q91, Q92, Q93]), "oppositeDirection" : true, "depth" : 5 * mm});
        }
    });
